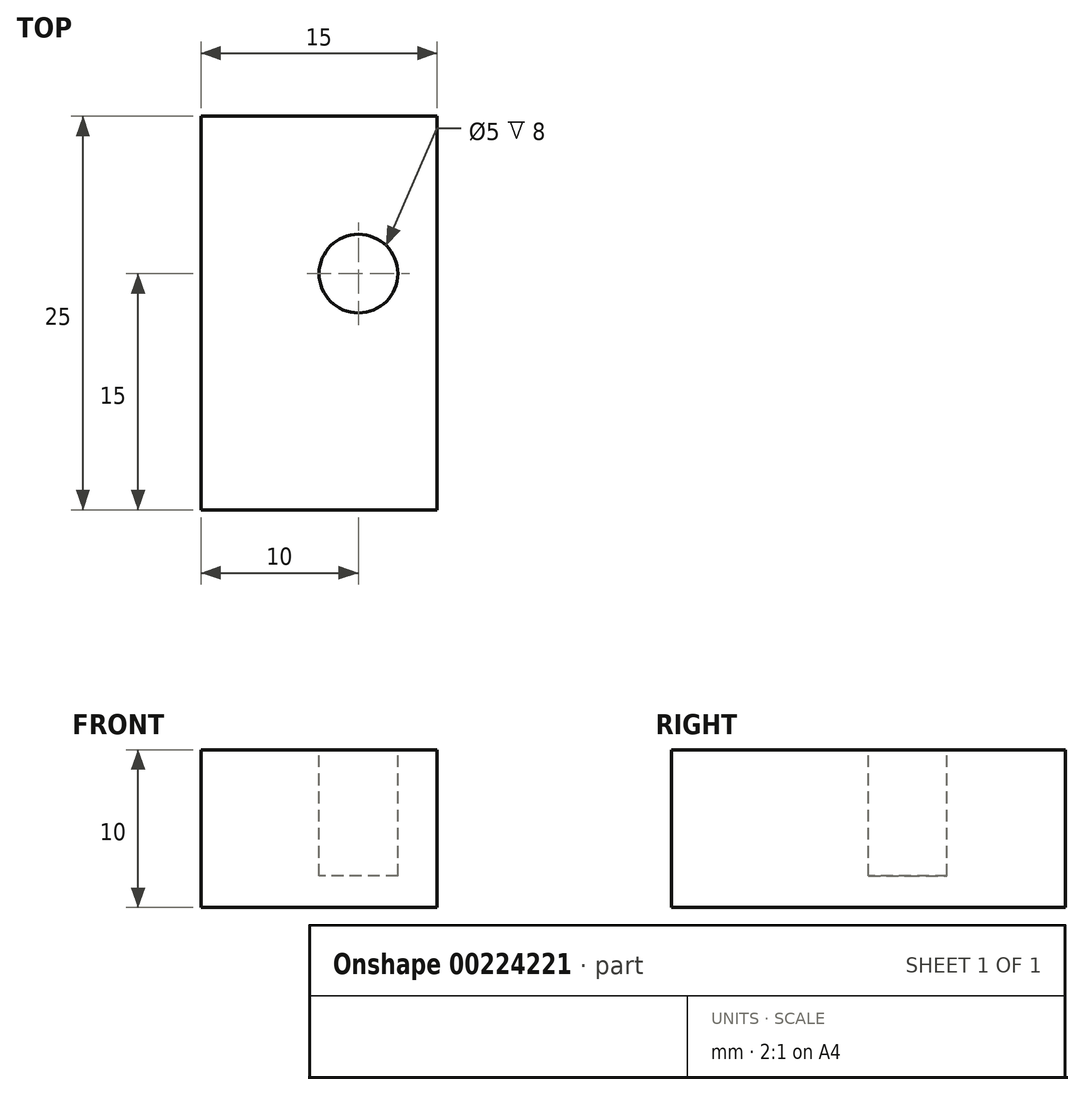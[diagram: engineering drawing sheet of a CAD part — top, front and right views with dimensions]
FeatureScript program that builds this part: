
annotation { "Feature Type Name" : "Feature", "Feature Type Description" : "" }
export const myFeature = defineFeature(function(context is Context, id is Id, definition is map)
    precondition{}
    {
        {
            assignVariable(context, id + "F0", {"name" : "HOLE_DEPTH", "anyValue" : 8});
        }
        {
            var Q0;
            Q0=qCreatedBy(makeId("Front.planeOp"),FACE);
            var sketch = newSketch(context, id + "F1", { "sketchPlane" : qUnion([Q0])});
            skLineSegment(sketch, "E0.bottom", {"start": v(-7.5, 5) * mm, "end": v(7.5, 5) * mm});
            skLineSegment(sketch, "E0.top", {"start": v(-7.5, -5) * mm, "end": v(7.5, -5) * mm});
            skLineSegment(sketch, "E0.left", {"start": v(-7.5, 5) * mm, "end": v(-7.5, -5) * mm});
            skLineSegment(sketch, "E0.right", {"start": v(7.5, 5) * mm, "end": v(7.5, -5) * mm});
            skSolve(sketch);
        }
        {
            var Q0;
            Q0=makeQuery(id+"F1.imprint","IMPRINT",FACE,{"disambiguationData":[TD([[makeQuery(id+"F1.imprint","IMPRINT",EDGE,{"derivedFrom":sQuery(id+"F1.wireOp",EDGE,"E0.bottom")}),-1.0]])]});
            extrude(context, id + "F2", {"entities" : qUnion([Q0]), "depth" : 25 * mm});
        }
        {
            var Q0;
            Q0=makeQuery(id+"F2.opExtrude","SWEPT_FACE",FACE,{"disambiguationData":[OSD([sQuery(id+"F1.wireOp",EDGE,"E0.bottom")])]});
            var sketch = newSketch(context, id + "F3", { "sketchPlane" : qUnion([Q0])});
            skCircle(sketch, "E1", {"center": v(2.5, -10) * mm, "radius": 2.5 * mm});
            skSolve(sketch);
        }
        {
            var Q0;
            Q0=makeQuery(id+"F3.imprint","IMPRINT",FACE,{"disambiguationData":[TD([[makeQuery(id+"F3.imprint","IMPRINT",EDGE,{"derivedFrom":sQuery(id+"F3.wireOp",EDGE,"E1")}),1.0]])]});
            extrude(context, id + "F4", {"entities" : qUnion([Q0]), "operationType" : NewBodyOperationType.REMOVE, "oppositeDirection" : true, "depth" : (getVariable(context, 'HOLE_DEPTH')) * mm});
        }
    });
